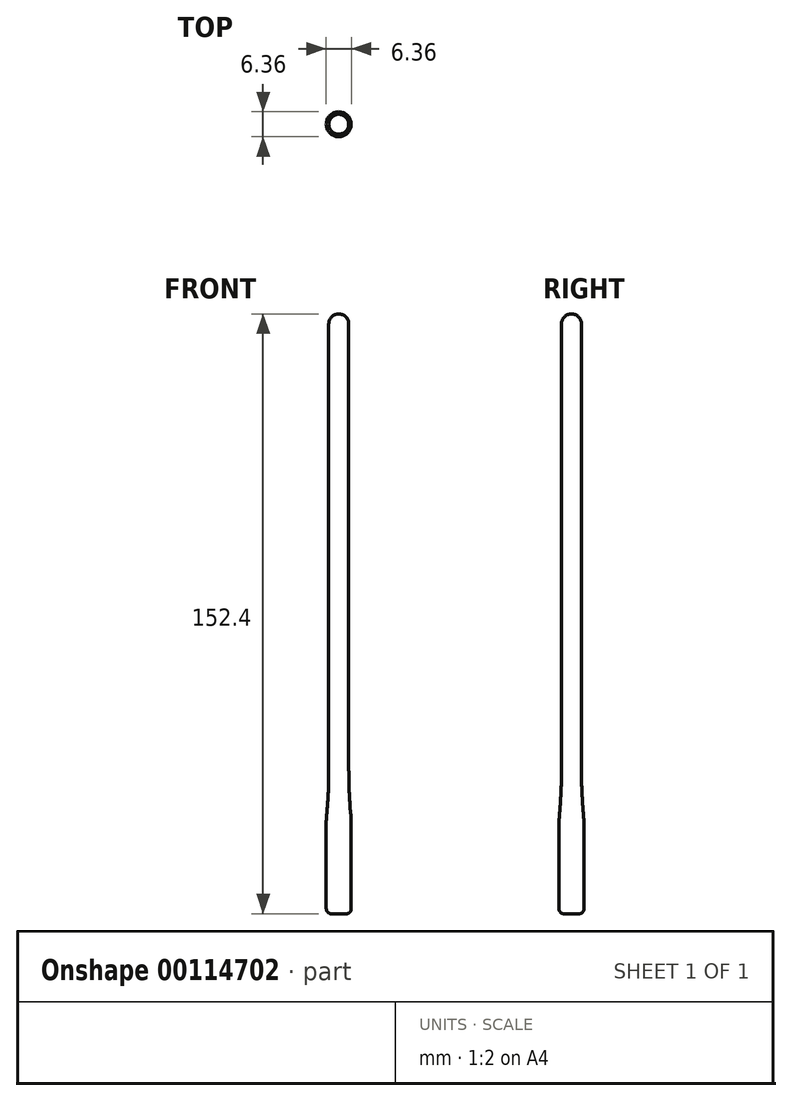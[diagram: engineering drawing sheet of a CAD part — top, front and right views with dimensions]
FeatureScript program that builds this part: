
annotation { "Feature Type Name" : "Feature", "Feature Type Description" : "" }
export const myFeature = defineFeature(function(context is Context, id is Id, definition is map)
    precondition{}
    {
        {
            var Q0;
            Q0=qCreatedBy(makeId("Top.planeOp"),FACE);
            var sketch = newSketch(context, id + "F0", { "sketchPlane" : qUnion([Q0])});
            skCircle(sketch, "E0", {"center": v(0, 0) * mm, "radius": 2.54 * mm});
            skCircle(sketch, "E1", {"center": v(0, 0) * mm, "radius": 3.18 * mm});
            skSolve(sketch);
        }
        {
            var Q0;
            Q0=makeQuery(id+"F0.imprint","IMPRINT",FACE,{"disambiguationData":[TD([[makeQuery(id+"F0.imprint","IMPRINT",EDGE,{"derivedFrom":sQuery(id+"F0.wireOp",EDGE,"E0")}),1.0]])]});
            extrude(context, id + "F1", {"entities" : qUnion([Q0]), "depth" : 152.4 * mm});
        }
        {
            var Q0;
            Q0=makeQuery(id+"F1.opExtrude","CAP_EDGE",EDGE,{"disambiguationData":[OSD([sQuery(id+"F0.wireOp",EDGE,"E0")])],"isStart":false});
            fillet(context, id + "F2", {"entities" : qUnion([Q0]), "radius" : 2.54 * mm, "tangentPropagation" : true, "allowEdgeOverflow" : false});
        }
        {
            var Q0;
            Q0=makeQuery(id+"F0.imprint","IMPRINT",FACE,{"disambiguationData":[TD([[makeQuery(id+"F0.imprint","IMPRINT",EDGE,{"derivedFrom":sQuery(id+"F0.wireOp",EDGE,"E0")}),-1.0]])]});
            extrude(context, id + "F3", {"entities" : qUnion([Q0]), "operationType" : NewBodyOperationType.ADD, "depth" : 25.4 * mm});
        }
        {
            var Q0;
            Q0=makeQuery(id+"F3.opExtrude","CAP_EDGE",EDGE,{"disambiguationData":[OSD([sQuery(id+"F0.wireOp",EDGE,"E1")])],"isStart":false});
            fillet(context, id + "F4", {"entities" : qUnion([Q0]), "radius" : 2.54 * mm, "tangentPropagation" : true, "allowEdgeOverflow" : false});
        }
        {
            var Q0;
            Q0=makeQuery(id+"F4.opFillet","BLEND_EDGE",EDGE,{"blendedFrom":[makeQuery(id+"F3.opExtrude","CAP_EDGE",EDGE,{"disambiguationData":[OSD([sQuery(id+"F0.wireOp",EDGE,"E1")])],"isStart":false}),makeQuery(id+"F1.opExtrude","SWEPT_FACE",FACE,{"disambiguationData":[OSD([sQuery(id+"F0.wireOp",EDGE,"E0")])]})],"blendedInto":[makeQuery(id+"F1.opExtrude","SWEPT_FACE",FACE,{"disambiguationData":[OSD([sQuery(id+"F0.wireOp",EDGE,"E0")])]})]});
            fillet(context, id + "F5", {"entities" : qUnion([Q0]), "radius" : 127 * mm, "tangentPropagation" : true, "allowEdgeOverflow" : false});
        }
        {
            var Q0;
            Q0=makeQuery(id+"F3.opExtrude","CAP_EDGE",EDGE,{"disambiguationData":[OSD([sQuery(id+"F0.wireOp",EDGE,"E1")])],"isStart":true});
            fillet(context, id + "F6", {"entities" : qUnion([Q0]), "radius" : 1.27 * mm, "tangentPropagation" : true, "allowEdgeOverflow" : false});
        }
    });
